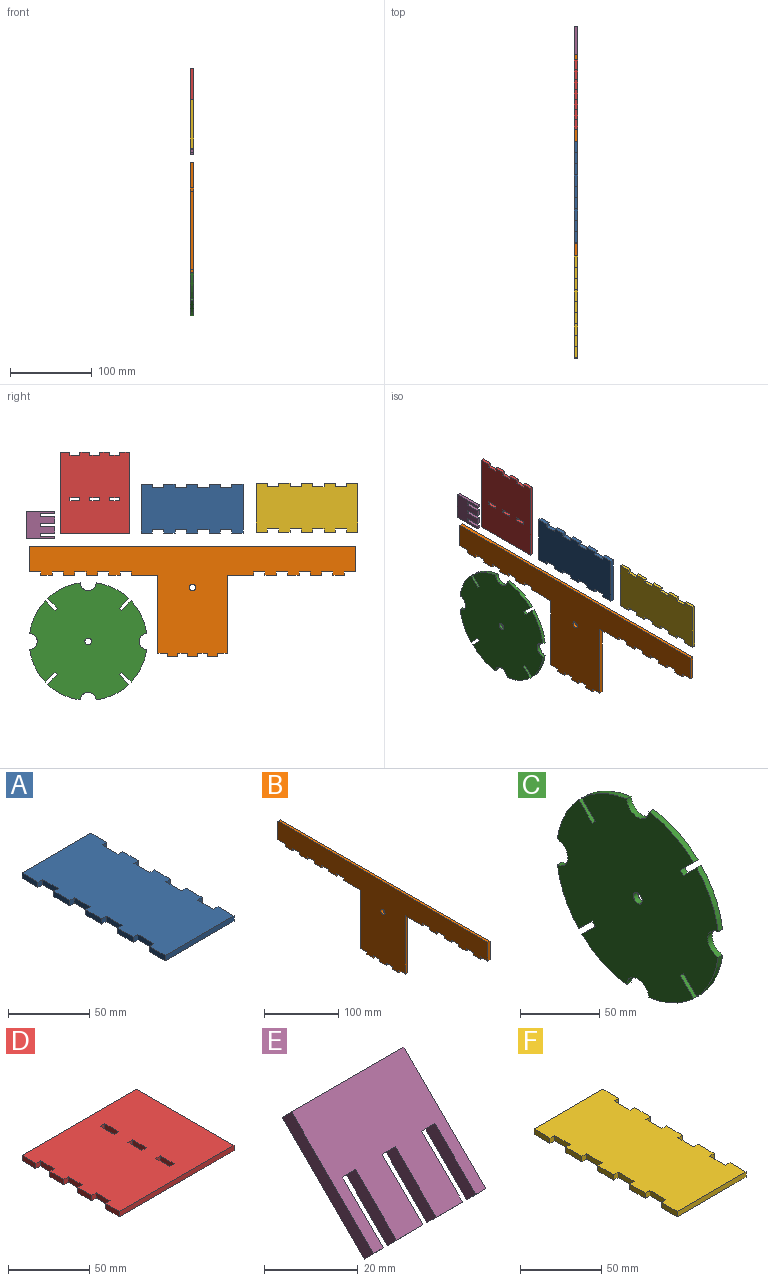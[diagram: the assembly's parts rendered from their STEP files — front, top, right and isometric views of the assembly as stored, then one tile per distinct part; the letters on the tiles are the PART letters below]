
ASSEMBLY  parts=6 mates=5
PART A: 38 faces, bbox 60x125x4 mm
  f0: plane 13.89x4mm, normal (1,0,0), area 55.6mm2, adj f4,f5,f34,f35
  f1: plane 13.89x4mm, normal (1,0,0), area 55.6mm2, adj f4,f5,f31,f32
  f2: plane 13.89x4mm, normal (1,0,0), area 55.6mm2, adj f4,f5,f28,f29
  f3: plane 13.89x4mm, normal (1,0,0), area 55.6mm2, adj f4,f5,f12,f26
  f4: plane 125x60mm, normal (0,0,1), area 7055.6mm2, adj f0,f1,f2,f3,f6,f7,f8,f9
  f5: plane 125x60mm, normal (0,0,-1), area 7055.6mm2, adj f0,f1,f2,f3,f6,f7,f8,f9
  f6: plane 13.89x4mm, normal (-1,0,0), area 55.6mm2, adj f4,f5,f22,f24
  f7: plane 13.89x4mm, normal (-1,0,0), area 55.6mm2, adj f4,f5,f19,f21
  f8: plane 13.89x4mm, normal (-1,0,0), area 55.6mm2, adj f4,f5,f16,f18
  f9: plane 13.89x4mm, normal (-1,0,0), area 55.6mm2, adj f4,f5,f12,f15
  f10: plane 60x4mm, normal (0,1,0), area 240mm2, adj f4,f5,f11,f13
  f11: plane 13.89x4mm, normal (-1,0,0), area 55.6mm2, adj f4,f5,f10,f25
  f12: plane 60x4mm, normal (0,-1,0), area 240mm2, adj f3,f4,f5,f9
  f13: plane 13.89x4mm, normal (1,0,0), area 55.6mm2, adj f4,f5,f10,f37
  f14: plane 13.89x4mm, normal (-1,0,0), area 55.6mm2, adj f4,f5,f15,f16
  f15: plane 4x4mm, normal (0,1,0), area 16mm2, adj f4,f5,f9,f14
  f16: plane 4x4mm, normal (0,-1,0), area 16mm2, adj f4,f5,f8,f14
  f17: plane 13.89x4mm, normal (-1,0,0), area 55.6mm2, adj f4,f5,f18,f19
  f18: plane 4x4mm, normal (0,1,0), area 16mm2, adj f4,f5,f8,f17
  f19: plane 4x4mm, normal (0,-1,0), area 16mm2, adj f4,f5,f7,f17
  f20: plane 13.89x4mm, normal (-1,0,0), area 55.6mm2, adj f4,f5,f21,f22
  f21: plane 4x4mm, normal (0,1,0), area 16mm2, adj f4,f5,f7,f20
  f22: plane 4x4mm, normal (0,-1,0), area 16mm2, adj f4,f5,f6,f20
  f23: plane 13.89x4mm, normal (-1,0,0), area 55.6mm2, adj f4,f5,f24,f25
  f24: plane 4x4mm, normal (0,1,0), area 16mm2, adj f4,f5,f6,f23
  f25: plane 4x4mm, normal (0,-1,0), area 16mm2, adj f4,f5,f11,f23
  f26: plane 4x4mm, normal (0,1,0), area 16mm2, adj f3,f4,f5,f27
  f27: plane 13.89x4mm, normal (1,0,0), area 55.6mm2, adj f4,f5,f26,f28
  f28: plane 4x4mm, normal (0,-1,0), area 16mm2, adj f2,f4,f5,f27
  f29: plane 4x4mm, normal (0,1,0), area 16mm2, adj f2,f4,f5,f30
  f30: plane 13.89x4mm, normal (1,0,0), area 55.6mm2, adj f4,f5,f29,f31
  f31: plane 4x4mm, normal (0,-1,0), area 16mm2, adj f1,f4,f5,f30
  f32: plane 4x4mm, normal (0,1,0), area 16mm2, adj f1,f4,f5,f33
  f33: plane 13.89x4mm, normal (1,0,0), area 55.6mm2, adj f4,f5,f32,f34
  f34: plane 4x4mm, normal (0,-1,0), area 16mm2, adj f0,f4,f5,f33
  f35: plane 4x4mm, normal (0,1,0), area 16mm2, adj f0,f4,f5,f36
  f36: plane 13.89x4mm, normal (1,0,0), area 55.6mm2, adj f4,f5,f35,f37
  f37: plane 4x4mm, normal (0,-1,0), area 16mm2, adj f4,f5,f13,f36
PART B: 59 faces, bbox 4x400x135 mm
  f0: plane 12.34x4mm, normal (0,0,-1), area 49.4mm2, adj f3,f4,f50,f58
  f1: plane 12.34x4mm, normal (0,0,-1), area 49.4mm2, adj f3,f4,f54,f56
  f2: plane 12.34x4mm, normal (0,0,-1), area 49.4mm2, adj f3,f4,f51,f53
  f3: plane 400x135mm, normal (-1,0,0), area 21709.5mm2, adj f0,f1,f2,f5,f6,f7,f8,f9
  f4: plane 400x135mm, normal (1,0,0), area 21709.5mm2, adj f0,f1,f2,f5,f6,f7,f8,f9
  f5: plane 14.09x4mm, normal (0,0,-1), area 56.4mm2, adj f3,f4,f42,f46
  f6: plane 14.09x4mm, normal (0,0,-1), area 56.4mm2, adj f3,f4,f39,f43
  f7: plane 14.09x4mm, normal (0,0,-1), area 56.4mm2, adj f3,f4,f40,f48
  f8: plane 14.09x4mm, normal (0,0,-1), area 56.4mm2, adj f3,f4,f37,f45
  f9: plane 31x4mm, normal (0,1,0), area 124mm2, adj f3,f4,f17,f47
  f10: plane 14.09x4mm, normal (0,0,-1), area 56.4mm2, adj f3,f4,f22,f34
  f11: plane 32.6x4mm, normal (0,0,-1), area 130.4mm2, adj f3,f4,f19,f32
  f12: plane 14.09x4mm, normal (0,0,-1), area 56.4mm2, adj f3,f4,f29,f31
  f13: plane 14.09x4mm, normal (0,0,-1), area 56.4mm2, adj f3,f4,f26,f28
  f14: plane 14.09x4mm, normal (0,0,-1), area 56.4mm2, adj f3,f4,f23,f25
  f15: plane 31x4mm, normal (0,-1,0), area 124mm2, adj f3,f4,f17,f33
  f16: plane 32.6x4mm, normal (0,0,-1), area 130.4mm2, adj f3,f4,f18,f36
  f17: plane 400x4mm, normal (0,0,1), area 1600mm2, adj f3,f4,f9,f15
  f18: plane 96x4mm, normal (0,1,0), area 384mm2, adj f3,f4,f16,f55
  f19: plane 96x4mm, normal (0,-1,0), area 384mm2, adj f3,f4,f11,f57
  f20: cylinder r=4mm len=8mm, axis (1,0,0), area 100.5mm2, adj f3,f4
  f21: plane 13.69x4mm, normal (0,0,-1), area 54.8mm2, adj f3,f4,f22,f23
  f22: plane 4x4mm, normal (0,1,0), area 16mm2, adj f3,f4,f10,f21
  f23: plane 4x4mm, normal (0,-1,0), area 16mm2, adj f3,f4,f14,f21
  f24: plane 13.69x4mm, normal (0,0,-1), area 54.8mm2, adj f3,f4,f25,f26
  f25: plane 4x4mm, normal (0,1,0), area 16mm2, adj f3,f4,f14,f24
  f26: plane 4x4mm, normal (0,-1,0), area 16mm2, adj f3,f4,f13,f24
  f27: plane 13.69x4mm, normal (0,0,-1), area 54.8mm2, adj f3,f4,f28,f29
  f28: plane 4x4mm, normal (0,1,0), area 16mm2, adj f3,f4,f13,f27
  f29: plane 4x4mm, normal (0,-1,0), area 16mm2, adj f3,f4,f12,f27
  f30: plane 13.69x4mm, normal (0,0,-1), area 54.8mm2, adj f3,f4,f31,f32
  f31: plane 4x4mm, normal (0,1,0), area 16mm2, adj f3,f4,f12,f30
  f32: plane 4x4mm, normal (0,-1,0), area 16mm2, adj f3,f4,f11,f30
  f33: plane 13.79x4mm, normal (0,0,-1), area 55.2mm2, adj f3,f4,f15,f34
  f34: plane 4x4mm, normal (0,-1,0), area 16mm2, adj f3,f4,f10,f33
  f35: plane 13.69x4mm, normal (0,0,-1), area 54.8mm2, adj f3,f4,f36,f37
  f36: plane 4x4mm, normal (0,1,0), area 16mm2, adj f3,f4,f16,f35
  f37: plane 4x4mm, normal (0,-1,0), area 16mm2, adj f3,f4,f8,f35
  f38: plane 13.69x4mm, normal (0,0,-1), area 54.8mm2, adj f3,f4,f39,f40
  f39: plane 4x4mm, normal (0,1,0), area 16mm2, adj f3,f4,f6,f38
  f40: plane 4x4mm, normal (0,-1,0), area 16mm2, adj f3,f4,f7,f38
  f41: plane 13.69x4mm, normal (0,0,-1), area 54.8mm2, adj f3,f4,f42,f43
  f42: plane 4x4mm, normal (0,1,0), area 16mm2, adj f3,f4,f5,f41
  f43: plane 4x4mm, normal (0,-1,0), area 16mm2, adj f3,f4,f6,f41
  f44: plane 13.69x4mm, normal (0,0,-1), area 54.8mm2, adj f3,f4,f45,f46
  f45: plane 4x4mm, normal (0,1,0), area 16mm2, adj f3,f4,f8,f44
  f46: plane 4x4mm, normal (0,-1,0), area 16mm2, adj f3,f4,f5,f44
  f47: plane 13.79x4mm, normal (0,0,-1), area 55.2mm2, adj f3,f4,f9,f48
  f48: plane 4x4mm, normal (0,1,0), area 16mm2, adj f3,f4,f7,f47
  f49: plane 11.94x4mm, normal (0,0,-1), area 47.8mm2, adj f3,f4,f50,f51
  f50: plane 4x4mm, normal (0,1,0), area 16mm2, adj f0,f3,f4,f49
  f51: plane 4x4mm, normal (0,-1,0), area 16mm2, adj f2,f3,f4,f49
  f52: plane 11.94x4mm, normal (0,0,-1), area 47.8mm2, adj f3,f4,f53,f54
  f53: plane 4x4mm, normal (0,1,0), area 16mm2, adj f2,f3,f4,f52
  f54: plane 4x4mm, normal (0,-1,0), area 16mm2, adj f1,f3,f4,f52
  f55: plane 12.04x4mm, normal (0,0,-1), area 48.2mm2, adj f3,f4,f18,f56
  f56: plane 4x4mm, normal (0,1,0), area 16mm2, adj f1,f3,f4,f55
  f57: plane 12.04x4mm, normal (0,0,-1), area 48.2mm2, adj f3,f4,f19,f58
  f58: plane 4x4mm, normal (0,-1,0), area 16mm2, adj f0,f3,f4,f57
PART C: 27 faces, bbox 4x143.6x143.6 mm
  f0: cylinder r=72.5mm len=39.86mm, axis (-1,0,0), area 179.7mm2, adj f2,f5,f13,f23
  f1: cylinder r=72.5mm len=39.86mm, axis (-1,0,0), area 179.7mm2, adj f2,f5,f10,f14
  f2: plane 143.62x143.62mm, normal (-1,0,0), area 15581mm2, adj f0,f1,f3,f4,f6,f7,f8,f9
  f3: cylinder r=72.5mm len=39.86mm, axis (-1,0,0), area 179.7mm2, adj f2,f5,f12,f20
  f4: cylinder r=72.5mm len=39.86mm, axis (-1,0,0), area 179.7mm2, adj f2,f5,f11,f17
  f5: plane 143.62x143.62mm, normal (1,0,0), area 15581mm2, adj f0,f1,f3,f4,f6,f7,f8,f9
  f6: cylinder r=72.5mm len=39.86mm, axis (-1,0,0), area 179.7mm2, adj f2,f5,f12,f24
  f7: cylinder r=72.5mm len=39.86mm, axis (-1,0,0), area 179.7mm2, adj f2,f5,f13,f15
  f8: cylinder r=72.5mm len=39.86mm, axis (-1,0,0), area 179.7mm2, adj f2,f5,f11,f21
  f9: cylinder r=72.5mm len=39.86mm, axis (-1,0,0), area 179.7mm2, adj f2,f5,f10,f18
  f10: cylinder r=10mm len=19.95mm, axis (1,0,0), area 120.1mm2, adj f1,f2,f5,f9
  f11: cylinder r=10mm len=19.95mm, axis (1,0,0), area 120.1mm2, adj f2,f4,f5,f8
  f12: cylinder r=10mm len=19.95mm, axis (1,0,0), area 120.1mm2, adj f2,f3,f5,f6
  f13: cylinder r=10mm len=19.95mm, axis (1,0,0), area 120.1mm2, adj f0,f2,f5,f7
  f14: plane 12x12mm, normal (0,0.71,-0.71), area 67.9mm2, adj f1,f2,f5,f16
  f15: plane 12x12mm, normal (0,-0.71,0.71), area 67.9mm2, adj f2,f5,f7,f16
  f16: plane 4x2.83mm, normal (0,0.71,0.71), area 16mm2, adj f2,f5,f14,f15
  f17: plane 12x12mm, normal (0,0.71,0.71), area 67.9mm2, adj f2,f4,f5,f19
  f18: plane 12x12mm, normal (0,-0.71,-0.71), area 67.9mm2, adj f2,f5,f9,f19
  f19: plane 4x2.83mm, normal (0,-0.71,0.71), area 16mm2, adj f2,f5,f17,f18
  f20: plane 12x12mm, normal (0,-0.71,0.71), area 67.9mm2, adj f2,f3,f5,f22
  f21: plane 12x12mm, normal (0,0.71,-0.71), area 67.9mm2, adj f2,f5,f8,f22
  f22: plane 4x2.83mm, normal (0,-0.71,-0.71), area 16mm2, adj f2,f5,f20,f21
  f23: plane 12x12mm, normal (0,-0.71,-0.71), area 67.9mm2, adj f0,f2,f5,f25
  f24: plane 12x12mm, normal (0,0.71,0.71), area 67.9mm2, adj f2,f5,f6,f25
  f25: plane 4x2.83mm, normal (0,0.71,-0.71), area 16mm2, adj f2,f5,f23,f24
  f26: cylinder r=4mm len=8mm, axis (1,0,0), area 100.5mm2, adj f2,f5
PART D: 30 faces, bbox 100x85x4 mm
  f0: plane 100x85mm, normal (0,0,1), area 8208.6mm2, adj f2,f3,f4,f5,f6,f7,f8,f9
  f1: plane 100x85mm, normal (0,0,-1), area 8208.6mm2, adj f2,f3,f4,f5,f6,f7,f8,f9
  f2: plane 12.14x4mm, normal (-1,0,0), area 48.6mm2, adj f0,f1,f14,f16
  f3: plane 12.14x4mm, normal (-1,0,0), area 48.6mm2, adj f0,f1,f11,f13
  f4: plane 12.14x4mm, normal (-1,0,0), area 48.6mm2, adj f0,f1,f5,f10
  f5: plane 100x4mm, normal (0,-1,0), area 400mm2, adj f0,f1,f4,f8
  f6: plane 12.14x4mm, normal (-1,0,0), area 48.6mm2, adj f0,f1,f7,f17
  f7: plane 100x4mm, normal (0,1,0), area 400mm2, adj f0,f1,f6,f8
  f8: plane 85x4mm, normal (1,0,0), area 340mm2, adj f0,f1,f5,f7
  f9: plane 12.14x4mm, normal (-1,0,0), area 48.6mm2, adj f0,f1,f10,f11
  f10: plane 4x4mm, normal (0,1,0), area 16mm2, adj f0,f1,f4,f9
  f11: plane 4x4mm, normal (0,-1,0), area 16mm2, adj f0,f1,f3,f9
  f12: plane 12.14x4mm, normal (-1,0,0), area 48.6mm2, adj f0,f1,f13,f14
  f13: plane 4x4mm, normal (0,1,0), area 16mm2, adj f0,f1,f3,f12
  f14: plane 4x4mm, normal (0,-1,0), area 16mm2, adj f0,f1,f2,f12
  f15: plane 12.14x4mm, normal (-1,0,0), area 48.6mm2, adj f0,f1,f16,f17
  f16: plane 4x4mm, normal (0,1,0), area 16mm2, adj f0,f1,f2,f15
  f17: plane 4x4mm, normal (0,-1,0), area 16mm2, adj f0,f1,f6,f15
  f18: plane 12.14x4mm, normal (-1,0,0), area 48.6mm2, adj f0,f1,f19,f21
  f19: plane 4x4mm, normal (0,1,0), area 16mm2, adj f0,f1,f18,f20
  f20: plane 12.14x4mm, normal (1,0,0), area 48.6mm2, adj f0,f1,f19,f21
  f21: plane 4x4mm, normal (0,-1,0), area 16mm2, adj f0,f1,f18,f20
  f22: plane 12.14x4mm, normal (-1,0,0), area 48.6mm2, adj f0,f1,f23,f25
  f23: plane 4x4mm, normal (0,1,0), area 16mm2, adj f0,f1,f22,f24
  f24: plane 12.14x4mm, normal (1,0,0), area 48.6mm2, adj f0,f1,f23,f25
  f25: plane 4x4mm, normal (0,-1,0), area 16mm2, adj f0,f1,f22,f24
  f26: plane 12.14x4mm, normal (-1,0,0), area 48.6mm2, adj f0,f1,f27,f29
  f27: plane 4x4mm, normal (0,1,0), area 16mm2, adj f0,f1,f26,f28
  f28: plane 12.14x4mm, normal (1,0,0), area 48.6mm2, adj f0,f1,f27,f29
  f29: plane 4x4mm, normal (0,-1,0), area 16mm2, adj f0,f1,f26,f28
PART E: 18 faces, bbox 34x27.6x27.6 mm
  f0: plane 8x2.83mm, normal (0,-0.71,-0.71), area 32mm2, adj f3,f4,f13,f17
  f1: plane 8x2.83mm, normal (0,-0.71,-0.71), area 32mm2, adj f3,f4,f10,f12
  f2: plane 3x2.83mm, normal (0,-0.71,-0.71), area 12mm2, adj f3,f4,f5,f9
  f3: plane 34x24.75mm, normal (0,-0.71,0.71), area 980mm2, adj f0,f1,f2,f5,f6,f7,f8,f9
  f4: plane 34x24.75mm, normal (0,0.71,-0.71), area 980mm2, adj f0,f1,f2,f5,f6,f7,f8,f9
  f5: plane 27.58x27.58mm, normal (-1,0,0), area 140mm2, adj f2,f3,f4,f8
  f6: plane 3x2.83mm, normal (0,-0.71,-0.71), area 12mm2, adj f3,f4,f7,f15
  f7: plane 27.58x27.58mm, normal (1,0,0), area 140mm2, adj f3,f4,f6,f8
  f8: plane 34x2.83mm, normal (0,0.71,0.71), area 136mm2, adj f3,f4,f5,f7
  f9: plane 15.2x15.2mm, normal (1,0,0), area 70mm2, adj f2,f3,f4,f11
  f10: plane 15.2x15.2mm, normal (-1,0,0), area 70mm2, adj f1,f3,f4,f11
  f11: plane 4x2.83mm, normal (0,-0.71,-0.71), area 16mm2, adj f3,f4,f9,f10
  f12: plane 15.2x15.2mm, normal (1,0,0), area 70mm2, adj f1,f3,f4,f14
  f13: plane 15.2x15.2mm, normal (-1,0,0), area 70mm2, adj f0,f3,f4,f14
  f14: plane 4x2.83mm, normal (0,-0.71,-0.71), area 16mm2, adj f3,f4,f12,f13
  f15: plane 15.2x15.2mm, normal (-1,0,0), area 70mm2, adj f3,f4,f6,f16
  f16: plane 4x2.83mm, normal (0,-0.71,-0.71), area 16mm2, adj f3,f4,f15,f17
  f17: plane 15.2x15.2mm, normal (1,0,0), area 70mm2, adj f0,f3,f4,f16
PART F: 38 faces, bbox 60x125x4 mm
  f0: plane 13.89x4mm, normal (1,0,0), area 55.6mm2, adj f4,f5,f34,f35
  f1: plane 13.89x4mm, normal (1,0,0), area 55.6mm2, adj f4,f5,f31,f32
  f2: plane 13.89x4mm, normal (1,0,0), area 55.6mm2, adj f4,f5,f28,f29
  f3: plane 13.89x4mm, normal (1,0,0), area 55.6mm2, adj f4,f5,f12,f26
  f4: plane 125x60mm, normal (0,0,1), area 7055.6mm2, adj f0,f1,f2,f3,f6,f7,f8,f9
  f5: plane 125x60mm, normal (0,0,-1), area 7055.6mm2, adj f0,f1,f2,f3,f6,f7,f8,f9
  f6: plane 13.89x4mm, normal (-1,0,0), area 55.6mm2, adj f4,f5,f22,f24
  f7: plane 13.89x4mm, normal (-1,0,0), area 55.6mm2, adj f4,f5,f19,f21
  f8: plane 13.89x4mm, normal (-1,0,0), area 55.6mm2, adj f4,f5,f16,f18
  f9: plane 13.89x4mm, normal (-1,0,0), area 55.6mm2, adj f4,f5,f12,f15
  f10: plane 60x4mm, normal (0,1,0), area 240mm2, adj f4,f5,f11,f13
  f11: plane 13.89x4mm, normal (-1,0,0), area 55.6mm2, adj f4,f5,f10,f25
  f12: plane 60x4mm, normal (0,-1,0), area 240mm2, adj f3,f4,f5,f9
  f13: plane 13.89x4mm, normal (1,0,0), area 55.6mm2, adj f4,f5,f10,f37
  f14: plane 13.89x4mm, normal (-1,0,0), area 55.6mm2, adj f4,f5,f15,f16
  f15: plane 4x4mm, normal (0,1,0), area 16mm2, adj f4,f5,f9,f14
  f16: plane 4x4mm, normal (0,-1,0), area 16mm2, adj f4,f5,f8,f14
  f17: plane 13.89x4mm, normal (-1,0,0), area 55.6mm2, adj f4,f5,f18,f19
  f18: plane 4x4mm, normal (0,1,0), area 16mm2, adj f4,f5,f8,f17
  f19: plane 4x4mm, normal (0,-1,0), area 16mm2, adj f4,f5,f7,f17
  f20: plane 13.89x4mm, normal (-1,0,0), area 55.6mm2, adj f4,f5,f21,f22
  f21: plane 4x4mm, normal (0,1,0), area 16mm2, adj f4,f5,f7,f20
  f22: plane 4x4mm, normal (0,-1,0), area 16mm2, adj f4,f5,f6,f20
  f23: plane 13.89x4mm, normal (-1,0,0), area 55.6mm2, adj f4,f5,f24,f25
  f24: plane 4x4mm, normal (0,1,0), area 16mm2, adj f4,f5,f6,f23
  f25: plane 4x4mm, normal (0,-1,0), area 16mm2, adj f4,f5,f11,f23
  f26: plane 4x4mm, normal (0,1,0), area 16mm2, adj f3,f4,f5,f27
  f27: plane 13.89x4mm, normal (1,0,0), area 55.6mm2, adj f4,f5,f26,f28
  f28: plane 4x4mm, normal (0,-1,0), area 16mm2, adj f2,f4,f5,f27
  f29: plane 4x4mm, normal (0,1,0), area 16mm2, adj f2,f4,f5,f30
  f30: plane 13.89x4mm, normal (1,0,0), area 55.6mm2, adj f4,f5,f29,f31
  f31: plane 4x4mm, normal (0,-1,0), area 16mm2, adj f1,f4,f5,f30
  f32: plane 4x4mm, normal (0,1,0), area 16mm2, adj f1,f4,f5,f33
  f33: plane 13.89x4mm, normal (1,0,0), area 55.6mm2, adj f4,f5,f32,f34
  f34: plane 4x4mm, normal (0,-1,0), area 16mm2, adj f0,f4,f5,f33
  f35: plane 4x4mm, normal (0,1,0), area 16mm2, adj f0,f4,f5,f36
  f36: plane 13.89x4mm, normal (1,0,0), area 55.6mm2, adj f4,f5,f35,f37
  f37: plane 4x4mm, normal (0,-1,0), area 16mm2, adj f4,f5,f13,f36
PLACE A rot(axis=(0,1,0),90deg) t=(2.16,-205.47,107.56)mm
PLACE B t=(-23.84,-68.62,25.88)mm fixed
PLACE C t=(4.16,59.36,-40.34)mm
PLACE D rot(axis=(0,1,0),90deg) t=(102.16,51.38,146.91)mm
PLACE E rot(axis=(-0.36,0.86,0.36),98.4deg) t=(14.76,73.21,87.43)mm
PLACE F rot(axis=(0,1,0),90deg) t=(2.16,-71.45,108.6)mm
MATE planar C.f0 <-> B.f20  axis (1,0,0) through (6.16,59.36,-55.34)mm
MATE planar F.f4 <-> B.f4  axis (1,0,0) through (6.16,-208.95,108.6)mm
MATE planar D.f0 <-> B.f4  axis (1,0,0) through (6.16,69.6,172.91)mm
MATE planar E.f3 <-> B.f4  axis (1,0,0) through (6.16,135.6,87.43)mm
MATE planar A.f4 <-> B.f4  axis (1,0,0) through (6.16,-67.97,107.56)mm
